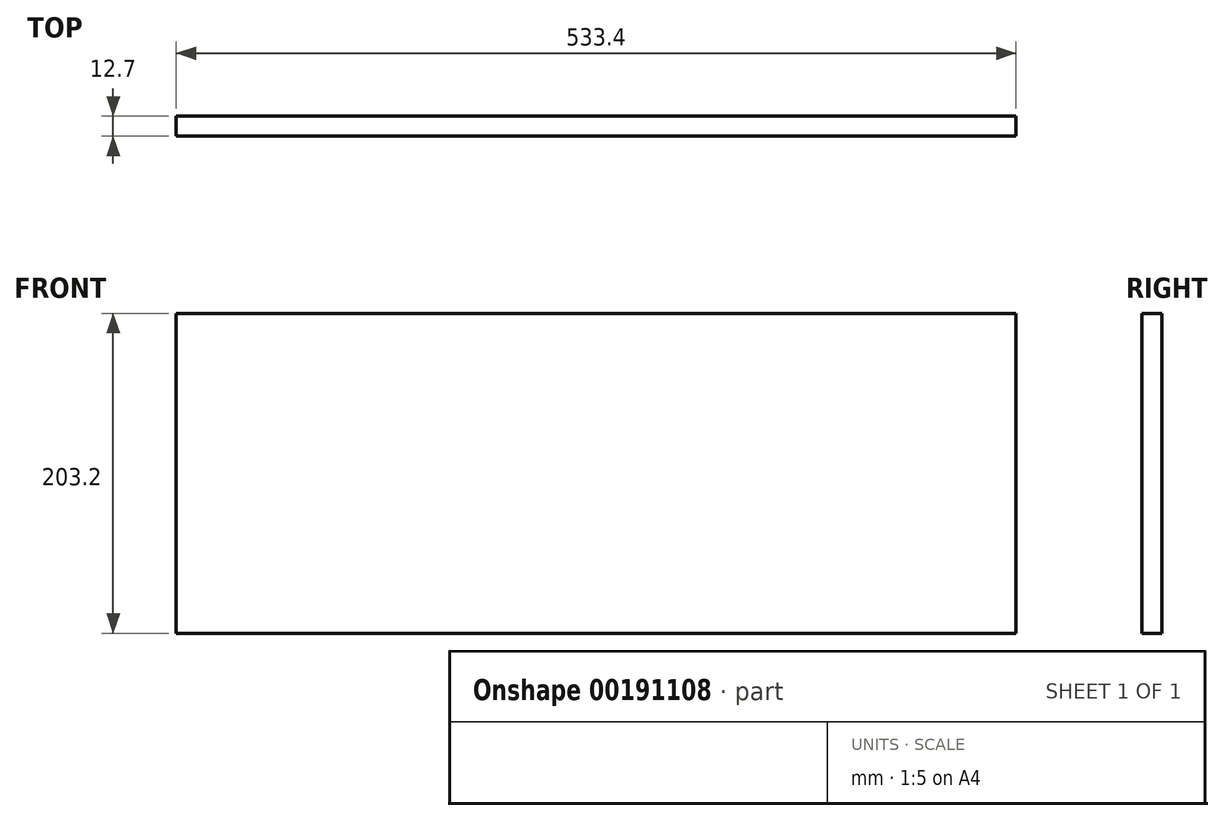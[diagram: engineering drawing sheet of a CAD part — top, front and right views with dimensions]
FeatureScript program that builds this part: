
annotation { "Feature Type Name" : "Feature", "Feature Type Description" : "" }
export const myFeature = defineFeature(function(context is Context, id is Id, definition is map)
    precondition{}
    {
        {
            var Q0;
            Q0=qCreatedBy(makeId("Front.planeOp"),FACE);
            var sketch = newSketch(context, id + "F0", { "sketchPlane" : qUnion([Q0])});
            skLineSegment(sketch, "E0.bottom", {"start": v(266.7, 101.6) * mm, "end": v(-266.7, 101.6) * mm});
            skLineSegment(sketch, "E0.top", {"start": v(266.7, -101.6) * mm, "end": v(-266.7, -101.6) * mm});
            skLineSegment(sketch, "E0.left", {"start": v(266.7, 101.6) * mm, "end": v(266.7, -101.6) * mm});
            skLineSegment(sketch, "E0.right", {"start": v(-266.7, 101.6) * mm, "end": v(-266.7, -101.6) * mm});
            skPoint(sketch, "E0.middle", {"position": v(0, 0) * mm});
            skSolve(sketch);
        }
        {
            var Q0;
            Q0 = qSketchRegion(id + "F0", true);
            extrude(context, id + "F1", {"entities" : qUnion([Q0]), "depth" : 12.7 * mm});
        }
    });
